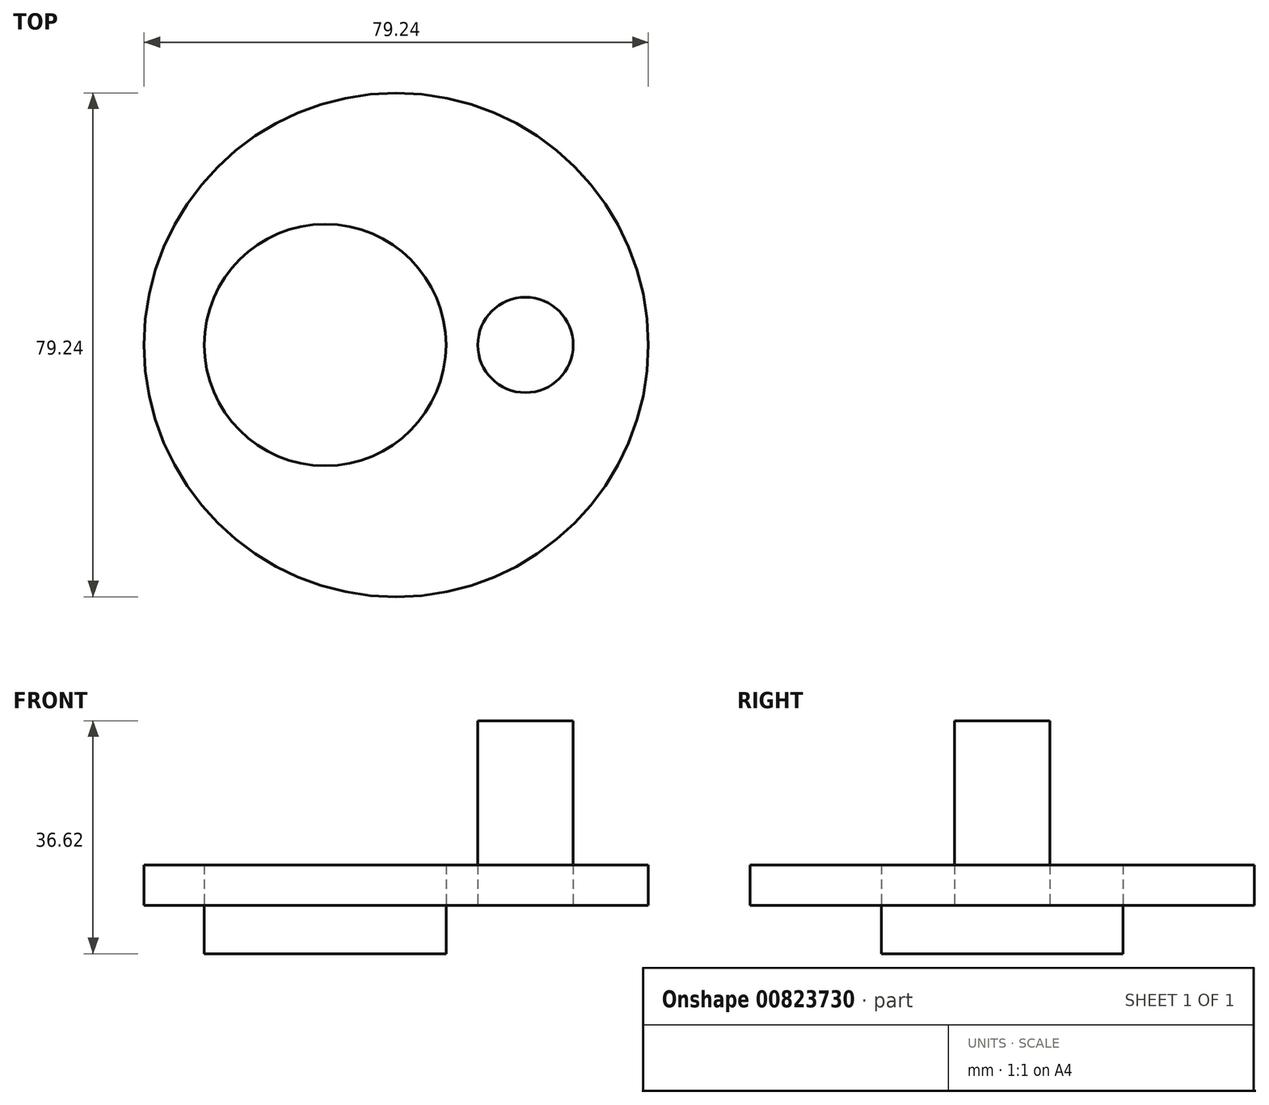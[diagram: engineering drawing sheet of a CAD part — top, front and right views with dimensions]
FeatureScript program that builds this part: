
annotation { "Feature Type Name" : "Feature", "Feature Type Description" : "" }
export const myFeature = defineFeature(function(context is Context, id is Id, definition is map)
    precondition{}
    {
        {
            var Q0;
            Q0=qCreatedBy(makeId("Top.planeOp"),FACE);
            var sketch = newSketch(context, id + "F0", { "sketchPlane" : qUnion([Q0])});
            skCircle(sketch, "E0", {"center": v(0, 0) * mm, "radius": 39.62 * mm});
            skCircle(sketch, "E1", {"center": v(-11.18, 0) * mm, "radius": 19 * mm});
            skCircle(sketch, "E2", {"center": v(20.32, 0) * mm, "radius": 7.5 * mm});
            skSolve(sketch);
        }
        {
            var Q0;
            Q0=qSketchRegion(id+"F0",true);
            extrude(context, id + "F1", {"entities" : qUnion([Q0]), "depth" : 6.35 * mm, "offsetDistance" : 25.4 * mm});
        }
        {
            var Q0;
            Q0=qCreatedBy(makeId("Top.planeOp"),FACE);
            var sketch = newSketch(context, id + "F2", { "sketchPlane" : qUnion([Q0])});
            skCircle(sketch, "E3.0", {"center": v(20.32, 0) * mm, "radius": 7.5 * mm});
            skSolve(sketch);
        }
        {
            var Q0;
            Q0=qSketchRegion(id+"F2",true);
            extrude(context, id + "F3", {"entities" : qUnion([Q0]), "depth" : 29 * mm, "offsetDistance" : 25.4 * mm});
        }
        {
            var Q0;
            Q0=qCreatedBy(makeId("Top.planeOp"),FACE);
            var sketch = newSketch(context, id + "F4", { "sketchPlane" : qUnion([Q0])});
            skCircle(sketch, "E4.0", {"center": v(-11.18, 0) * mm, "radius": 19 * mm});
            skSolve(sketch);
        }
        {
            var Q0;
            Q0=qSketchRegion(id+"F4",true);
            extrude(context, id + "F5", {"entities" : qUnion([Q0]), "oppositeDirection" : true, "depth" : 7.62 * mm, "offsetDistance" : 25.4 * mm});
        }
    });
